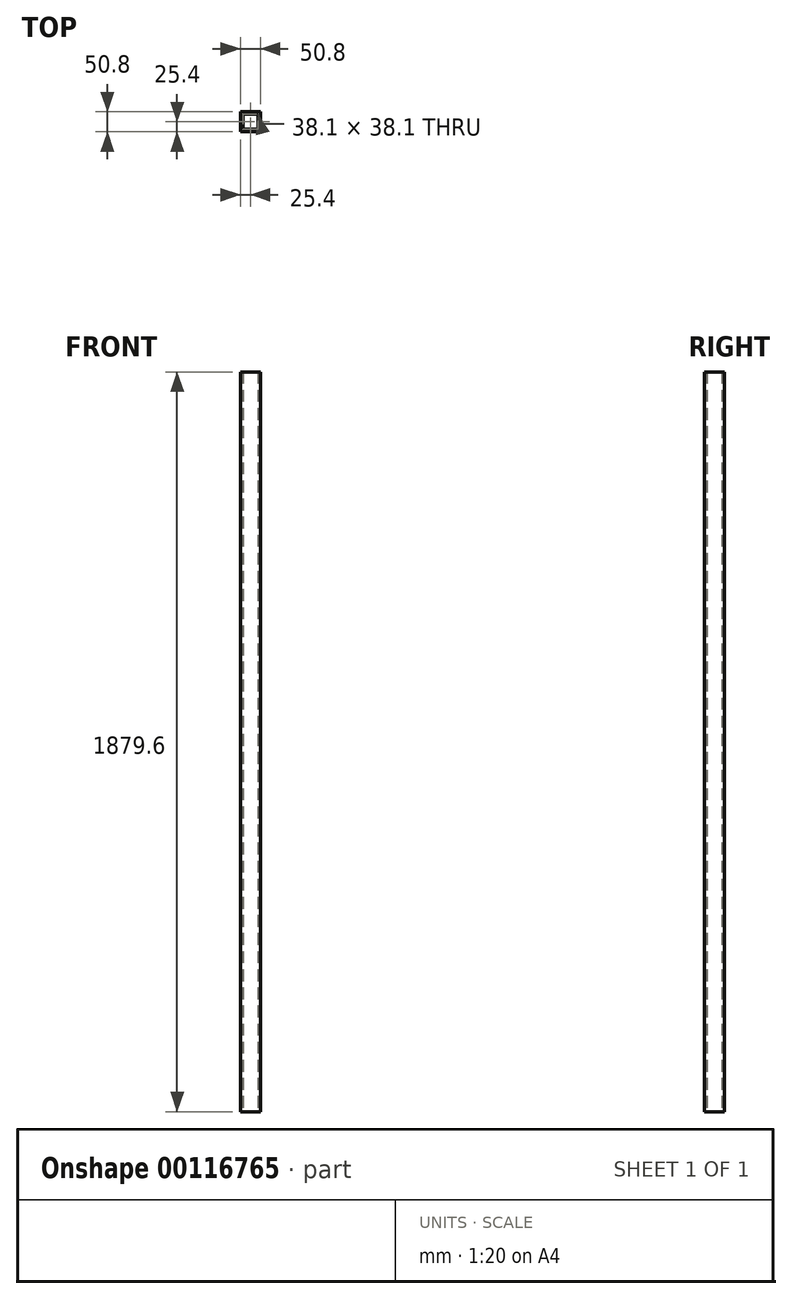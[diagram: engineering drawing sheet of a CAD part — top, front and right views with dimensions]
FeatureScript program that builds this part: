
annotation { "Feature Type Name" : "Feature", "Feature Type Description" : "" }
export const myFeature = defineFeature(function(context is Context, id is Id, definition is map)
    precondition{}
    {
        {
            var Q0;
            Q0=qCreatedBy(makeId("Top.planeOp"),FACE);
            var sketch = newSketch(context, id + "F0", { "sketchPlane" : qUnion([Q0])});
            skLineSegment(sketch, "E0", {"start": v(0, 0) * mm, "end": v(0, 50.8) * mm});
            skLineSegment(sketch, "E1", {"start": v(0, 50.8) * mm, "end": v(50.8, 50.8) * mm});
            skLineSegment(sketch, "E2", {"start": v(50.8, 50.8) * mm, "end": v(50.8, 0) * mm});
            skLineSegment(sketch, "E3", {"start": v(50.8, 0) * mm, "end": v(0, 0) * mm});
            skLineSegment(sketch, "E4", {"start": v(6.35, 6.35) * mm, "end": v(6.35, 44.45) * mm});
            skLineSegment(sketch, "E5", {"start": v(6.35, 44.45) * mm, "end": v(44.45, 44.45) * mm});
            skLineSegment(sketch, "E6", {"start": v(44.45, 44.45) * mm, "end": v(44.45, 6.35) * mm});
            skLineSegment(sketch, "E7", {"start": v(44.45, 6.35) * mm, "end": v(6.35, 6.35) * mm});
            skSolve(sketch);
        }
        {
            var Q0;
            Q0 = qSketchRegion(id + "F0", true);
            extrude(context, id + "F1", {"entities" : qUnion([Q0]), "depth" : 1879.6 * mm});
        }
    });
